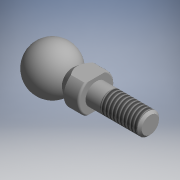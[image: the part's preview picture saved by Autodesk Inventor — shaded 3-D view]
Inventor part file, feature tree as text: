
AUTODESK INVENTOR PART (.ipt)
format: ipt  version: 2017.3 (Build 213256000, 256)  size: 143,872 bytes
history: native  units: mm (DEFAULTED — no unit token found)
features: other x7, sketch x2, revolve x1, thread x1, extrude x1
ambient origin geometry x8: Origin, YZ Plane, XZ Plane, XY Plane, X Axis, Y Axis, Z Axis, Center Point
bodies: Solid1 (feature_tree)
feature tree (12):
  revolve  "Revolution1"  [1 undecoded]
  thread  "Thread1"  [1 undecoded]
  extrude  "Extrusion1"  [1 undecoded]
  other  "shank_XY"
  other  "shank_YZ"
  other  "shank_ZX"
  other  "shank_X"
  other  "shank_Y"
  other  "shank_Z"
  other  "shank_Center"
  sketch  "Sketch_1"  dims[d0=360.0deg d1=10.3865mm d2=0.0mm d3=6.1mm d4=0.0mm]
  sketch  "Sketch_2"
note: 3 required parameter values undecoded (feature->parameter linkage not recoverable at this tier; creation-order binding heuristic only, values carry confidence <= 0.55)